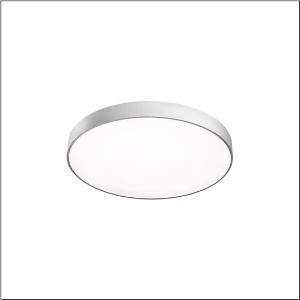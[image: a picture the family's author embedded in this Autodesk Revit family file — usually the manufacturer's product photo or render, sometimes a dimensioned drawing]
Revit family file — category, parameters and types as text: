
# Revit family: round_21_m_51mr36fm8321s
name_source: partatom
category: Lighting Fixtures
units: mm (PartAtom-declared; Revit-internal decimal feet)

## family parameters
Cut with Voids When Loaded = No
Host = Face
Light Source = No
Part Type = Normal
Room Calculation Point = No
Round Connector Dimension = Use Diameter
Shared = No

## types (1)
- --- (1 x LED, 8540 lm, 62.6 W, 3000K)
    Apparent Load = 63 VA
    CIE Flux Codes = 49 80 96 100 100
    Color Rendering = 80
    Color Temperature = 3000K
    Default Elevation = 1800 mm
    Description = Round 21 M, wall and ceiling luminaire, primary optical cover: cover, of PMMA, opal, light emission: direct distribution, primary light characteristic: symmetric, installation type: suspended mounting, surface-mounted, LED, rated luminous flux: 7.700lm, luminous efficacy: 127lm/W, light colour: 830, colour temperature: 3000K, with terminal, 3-pole, mains connection: 230V, AC, 50/60Hz, rated input power: 61W, housing, of aluminium, coated, silver, diameter: 600mm, height: 62mm, protection rating (complete): IP40, insulation class (complete): insulation class I (protective earthing), certification: CE, impact resistance: IK04, permissible operating ambient temperature: -10..+35°C, packaging unit: 1 piece
    Height = 87 mm
    Lamp = 1 x LED
    Lamp Light Flux = 8540 lm
    Lamp Power = 62.6 W
    Lamp count = 1
    Length = 600 mm
    Luminous efficacy = 136 lm/W
    Manufacturer = Siteco
    ModVariant = No
    Model = 51MR36FM8321S
    Mounting Place = Ceiling
    Mounting Type = Surface mounted
    Number of Poles = 1
    OnlyDefault = Yes
    Power Factor = 1
    Product Name = Round 21 M
    Product group = wall and ceiling luminaire
    ProductGroupID = 303
    Protection Class = Protection class I
    Protection Degree = IP 40
    RLX_Detail_Level = 1
    RLX_Emergency_Light_Flux = 0 lm
    RLX_Emergency_Type = 0
    RLX_Emergency_Type_DB = No
    RlxData = <blob elided: 17409 chars, md5=b9e7bef3>
    Socket = socket
    Standby Power = 0 W
    System Light Flux = 8540 lm
    System Power = 63 W
    Type Comments = factory setting: luminous flux: 100 % | (ON | ON | ON | ON) | 700 mA
    Type Image = l_1258303.jpg
    URL = http://relux.com
    VarID = @adj_001197
    Voltage = 0 V
    Weight = 0.00 kg
    Width = 0 mm  [stored 0 ft]

note: [stored X ft] marks values corroborated as IEEE doubles in the binary element streams (Revit-internal decimal feet)

## geometry (parser evidence)
native form markers: Blend x4, Sweep x12
no freeform markers — native parametric forms only
